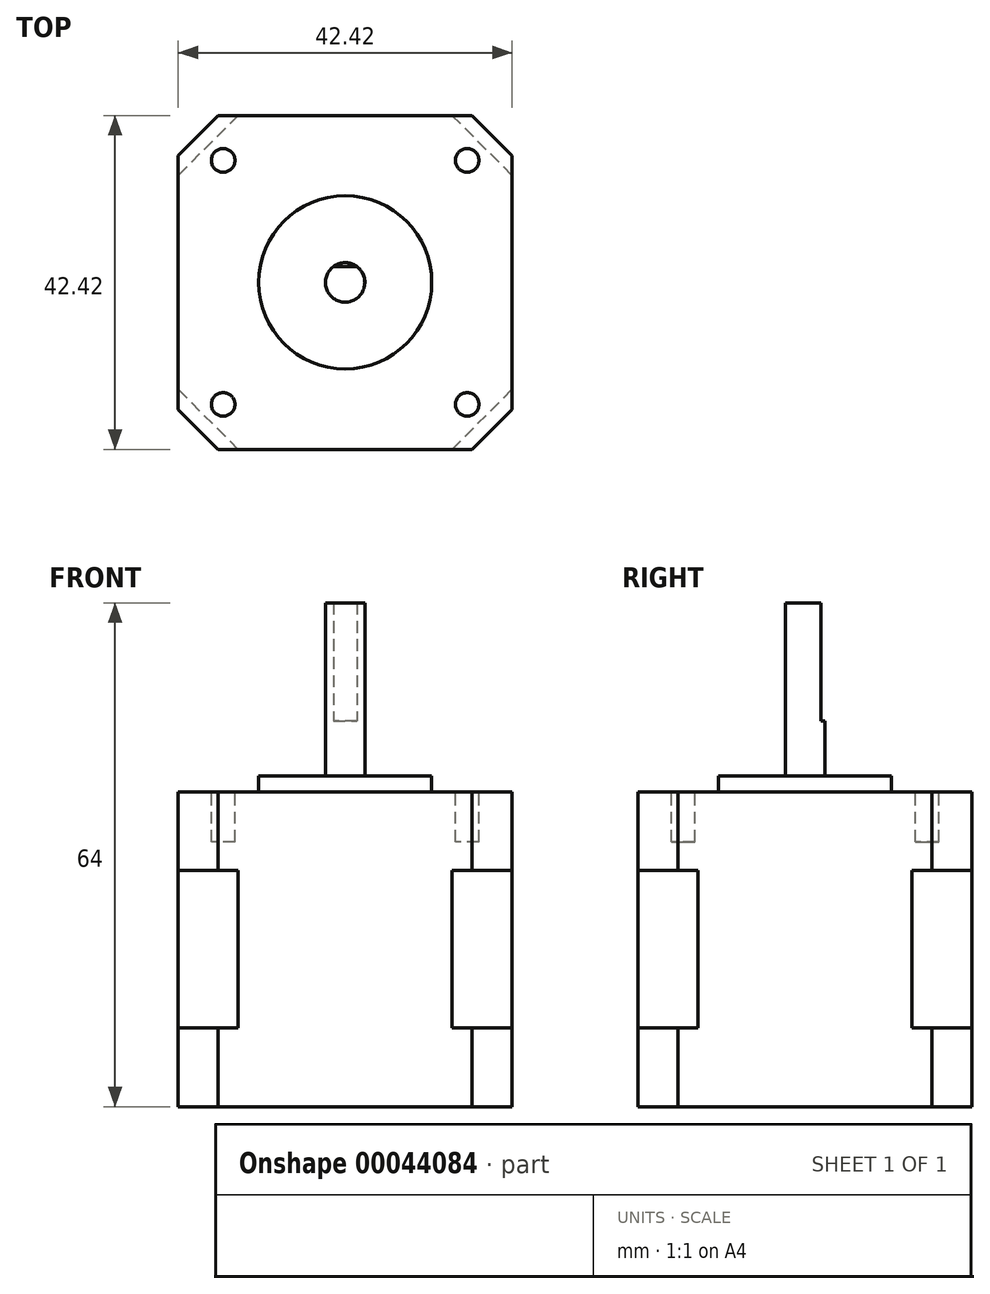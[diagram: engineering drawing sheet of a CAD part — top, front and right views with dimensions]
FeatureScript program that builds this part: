
annotation { "Feature Type Name" : "Feature", "Feature Type Description" : "" }
export const myFeature = defineFeature(function(context is Context, id is Id, definition is map)
    precondition{}
    {
        {
            var Q0;
            Q0=qCreatedBy(makeId("Top.planeOp"),FACE);
            var sketch = newSketch(context, id + "F0", { "sketchPlane" : qUnion([Q0])});
            skLineSegment(sketch, "E0.bottom", {"start": v(-21.2, 21.2) * mm, "end": v(21.2, 21.2) * mm});
            skLineSegment(sketch, "E0.top", {"start": v(-21.2, -21.2) * mm, "end": v(21.2, -21.2) * mm});
            skLineSegment(sketch, "E0.left", {"start": v(-21.2, 21.2) * mm, "end": v(-21.2, -21.2) * mm});
            skLineSegment(sketch, "E0.right", {"start": v(21.2, 21.2) * mm, "end": v(21.2, -21.2) * mm});
            skSolve(sketch);
        }
        {
            var Q0;
            Q0=makeQuery(id+"F0.imprint","IMPRINT",FACE,{"disambiguationData":[TD([[makeQuery(id+"F0.imprint","IMPRINT",EDGE,{"derivedFrom":sQuery(id+"F0.wireOp",EDGE,"E0.bottom")}),-1.0]])]});
            extrude(context, id + "F1", {"entities" : qUnion([Q0]), "depth" : 20 * mm, "symmetric" : true});
        }
        {
            var Q0;
            Q0=makeQuery(id+"F1.opExtrude","SWEPT_EDGE",EDGE,{"disambiguationData":[OSD([sQuery(id+"F0.wireOp",EDGE,"E0.bottom"),sQuery(id+"F0.wireOp",EDGE,"E0.right")])]});
            var Q1;
            Q1=makeQuery(id+"F1.opExtrude","SWEPT_EDGE",EDGE,{"disambiguationData":[OSD([sQuery(id+"F0.wireOp",EDGE,"E0.bottom"),sQuery(id+"F0.wireOp",EDGE,"E0.left")])]});
            var Q2;
            Q2=makeQuery(id+"F1.opExtrude","SWEPT_EDGE",EDGE,{"disambiguationData":[OSD([sQuery(id+"F0.wireOp",EDGE,"E0.top"),sQuery(id+"F0.wireOp",EDGE,"E0.left")])]});
            var Q3;
            Q3=makeQuery(id+"F1.opExtrude","SWEPT_EDGE",EDGE,{"disambiguationData":[OSD([sQuery(id+"F0.wireOp",EDGE,"E0.top"),sQuery(id+"F0.wireOp",EDGE,"E0.right")])]});
            chamfer(context, id + "F2", {"entities" : qUnion([Q0, Q1, Q2, Q3]), "width" : 7.62 * mm, "tangentPropagation" : true});
        }
        {
            var Q0;
            Q0=makeQuery(id+"F1.opExtrude","CAP_FACE",FACE,{"disambiguationData":[OSD([sQuery(id+"F0.wireOp",EDGE,"E0.bottom"),sQuery(id+"F0.wireOp",EDGE,"E0.top"),sQuery(id+"F0.wireOp",EDGE,"E0.left"),sQuery(id+"F0.wireOp",EDGE,"E0.right")])],"isStart":false});
            var sketch = newSketch(context, id + "F3", { "sketchPlane" : qUnion([Q0])});
            skLineSegment(sketch, "E1.bottom", {"start": v(-21.2, 21.2) * mm, "end": v(21.2, 21.2) * mm});
            skLineSegment(sketch, "E1.top", {"start": v(-21.2, -21.2) * mm, "end": v(21.2, -21.2) * mm});
            skLineSegment(sketch, "E1.left", {"start": v(-21.2, 21.2) * mm, "end": v(-21.2, -21.2) * mm});
            skLineSegment(sketch, "E1.right", {"start": v(21.2, 21.2) * mm, "end": v(21.2, -21.2) * mm});
            skSolve(sketch);
        }
        {
            var Q0;
            {var subQ0=sQuery(id+"F0.wireOp",EDGE,"E0.top");var subQ1=sQuery(id+"F0.wireOp",EDGE,"E0.right");var subQ2=sQuery(id+"F0.wireOp",EDGE,"E0.bottom");var subQ3=sQuery(id+"F0.wireOp",EDGE,"E0.left");var subQ4=makeQuery(id+"F1.opExtrude","CAP_FACE",FACE,{"disambiguationData":[OSD([subQ2,subQ0,subQ3,subQ1])],"isStart":false});var subQ8=makeQuery(id+"F2.opChamfer","BLEND_EDGE",EDGE,{"blendedFrom":[makeQuery(id+"F1.opExtrude","SWEPT_EDGE",EDGE,{"disambiguationData":[OSD([subQ2,subQ3])]}),subQ4],"blendedInto":[subQ4]});Q0=makeQuery(id+"F3.imprint","IMPRINT",FACE,{"disambiguationData":[TD([[makeQuery(id+"F3.imprint","IMPRINT",EDGE,{"derivedFrom":subQ8}),1.0]])]});}
            var Q1;
            {var subQ0=sQuery(id+"F0.wireOp",EDGE,"E0.bottom");var subQ1=sQuery(id+"F0.wireOp",EDGE,"E0.right");var subQ2=makeQuery(id+"F2.opChamfer","BLEND_EDGE",EDGE,{"blendedFrom":[makeQuery(id+"F1.opExtrude","SWEPT_EDGE",EDGE,{"disambiguationData":[OSD([subQ0,subQ1])]}),makeQuery(id+"F1.opExtrude","CAP_FACE",FACE,{"disambiguationData":[OSD([subQ0,sQuery(id+"F0.wireOp",EDGE,"E0.top"),sQuery(id+"F0.wireOp",EDGE,"E0.left"),subQ1])],"isStart":false})],"blendedInto":[makeQuery(id+"F1.opExtrude","CAP_FACE",FACE,{"disambiguationData":[OSD([subQ0,sQuery(id+"F0.wireOp",EDGE,"E0.top"),sQuery(id+"F0.wireOp",EDGE,"E0.left"),subQ1])],"isStart":false})]});Q1=makeQuery(id+"F3.imprint","IMPRINT",FACE,{"disambiguationData":[TD([[makeQuery(id+"F3.imprint","IMPRINT",EDGE,{"derivedFrom":subQ2}),-1.0]])]});}
            var Q2;
            {var subQ0=sQuery(id+"F0.wireOp",EDGE,"E0.bottom");var subQ1=sQuery(id+"F0.wireOp",EDGE,"E0.left");var subQ2=makeQuery(id+"F2.opChamfer","BLEND_EDGE",EDGE,{"blendedFrom":[makeQuery(id+"F1.opExtrude","SWEPT_EDGE",EDGE,{"disambiguationData":[OSD([subQ0,subQ1])]}),makeQuery(id+"F1.opExtrude","CAP_FACE",FACE,{"disambiguationData":[OSD([subQ0,sQuery(id+"F0.wireOp",EDGE,"E0.top"),subQ1,sQuery(id+"F0.wireOp",EDGE,"E0.right")])],"isStart":false})],"blendedInto":[makeQuery(id+"F1.opExtrude","CAP_FACE",FACE,{"disambiguationData":[OSD([subQ0,sQuery(id+"F0.wireOp",EDGE,"E0.top"),subQ1,sQuery(id+"F0.wireOp",EDGE,"E0.right")])],"isStart":false})]});Q2=makeQuery(id+"F3.imprint","IMPRINT",FACE,{"disambiguationData":[TD([[makeQuery(id+"F3.imprint","IMPRINT",EDGE,{"derivedFrom":subQ2}),-1.0]])]});}
            var Q3;
            {var subQ0=sQuery(id+"F0.wireOp",EDGE,"E0.top");var subQ1=sQuery(id+"F0.wireOp",EDGE,"E0.left");var subQ2=makeQuery(id+"F2.opChamfer","BLEND_EDGE",EDGE,{"blendedFrom":[makeQuery(id+"F1.opExtrude","SWEPT_EDGE",EDGE,{"disambiguationData":[OSD([subQ0,subQ1])]}),makeQuery(id+"F1.opExtrude","CAP_FACE",FACE,{"disambiguationData":[OSD([sQuery(id+"F0.wireOp",EDGE,"E0.bottom"),subQ0,subQ1,sQuery(id+"F0.wireOp",EDGE,"E0.right")])],"isStart":false})],"blendedInto":[makeQuery(id+"F1.opExtrude","CAP_FACE",FACE,{"disambiguationData":[OSD([sQuery(id+"F0.wireOp",EDGE,"E0.bottom"),subQ0,subQ1,sQuery(id+"F0.wireOp",EDGE,"E0.right")])],"isStart":false})]});Q3=makeQuery(id+"F3.imprint","IMPRINT",FACE,{"disambiguationData":[TD([[makeQuery(id+"F3.imprint","IMPRINT",EDGE,{"derivedFrom":subQ2}),-1.0]])]});}
            var Q4;
            {var subQ0=sQuery(id+"F0.wireOp",EDGE,"E0.top");var subQ1=sQuery(id+"F0.wireOp",EDGE,"E0.right");var subQ2=makeQuery(id+"F2.opChamfer","BLEND_EDGE",EDGE,{"blendedFrom":[makeQuery(id+"F1.opExtrude","SWEPT_EDGE",EDGE,{"disambiguationData":[OSD([subQ0,subQ1])]}),makeQuery(id+"F1.opExtrude","CAP_FACE",FACE,{"disambiguationData":[OSD([sQuery(id+"F0.wireOp",EDGE,"E0.bottom"),subQ0,sQuery(id+"F0.wireOp",EDGE,"E0.left"),subQ1])],"isStart":false})],"blendedInto":[makeQuery(id+"F1.opExtrude","CAP_FACE",FACE,{"disambiguationData":[OSD([sQuery(id+"F0.wireOp",EDGE,"E0.bottom"),subQ0,sQuery(id+"F0.wireOp",EDGE,"E0.left"),subQ1])],"isStart":false})]});Q4=makeQuery(id+"F3.imprint","IMPRINT",FACE,{"disambiguationData":[TD([[makeQuery(id+"F3.imprint","IMPRINT",EDGE,{"derivedFrom":subQ2}),-1.0]])]});}
            extrude(context, id + "F4", {"entities" : qUnion([Q0, Q1, Q2, Q3, Q4]), "operationType" : NewBodyOperationType.ADD, "depth" : 10 * mm});
        }
        {
            var Q0;
            Q0=makeQuery(id+"F4.opExtrude","SWEPT_EDGE",EDGE,{"disambiguationData":[OSD([sQuery(id+"F3.wireOp",EDGE,"E1.bottom"),sQuery(id+"F3.wireOp",EDGE,"E1.right")])]});
            var Q1;
            Q1=makeQuery(id+"F4.opExtrude","SWEPT_EDGE",EDGE,{"disambiguationData":[OSD([sQuery(id+"F3.wireOp",EDGE,"E1.bottom"),sQuery(id+"F3.wireOp",EDGE,"E1.left")])]});
            var Q2;
            Q2=makeQuery(id+"F4.opExtrude","SWEPT_EDGE",EDGE,{"disambiguationData":[OSD([sQuery(id+"F3.wireOp",EDGE,"E1.top"),sQuery(id+"F3.wireOp",EDGE,"E1.left")])]});
            var Q3;
            Q3=makeQuery(id+"F4.opExtrude","SWEPT_EDGE",EDGE,{"disambiguationData":[OSD([sQuery(id+"F3.wireOp",EDGE,"E1.top"),sQuery(id+"F3.wireOp",EDGE,"E1.right")])]});
            chamfer(context, id + "F5", {"entities" : qUnion([Q0, Q1, Q2, Q3]), "width" : 5.08 * mm, "tangentPropagation" : true});
        }
        {
            var Q0;
            Q0=makeQuery(id+"F1.opExtrude","CAP_FACE",FACE,{"disambiguationData":[OSD([sQuery(id+"F0.wireOp",EDGE,"E0.bottom"),sQuery(id+"F0.wireOp",EDGE,"E0.top"),sQuery(id+"F0.wireOp",EDGE,"E0.left"),sQuery(id+"F0.wireOp",EDGE,"E0.right")])],"isStart":true});
            var sketch = newSketch(context, id + "F6", { "sketchPlane" : qUnion([Q0])});
            skLineSegment(sketch, "E2.0.0", {"start": v(-16.13, 21.2) * mm, "end": v(16.13, 21.2) * mm});
            skLineSegment(sketch, "E2.0.1", {"start": v(16.13, 21.2) * mm, "end": v(21.2, 16.13) * mm});
            skLineSegment(sketch, "E2.0.2", {"start": v(21.2, -16.13) * mm, "end": v(21.2, 16.13) * mm});
            skLineSegment(sketch, "E2.0.3", {"start": v(21.2, -16.13) * mm, "end": v(16.13, -21.2) * mm});
            skLineSegment(sketch, "E2.0.4", {"start": v(-16.13, -21.2) * mm, "end": v(16.13, -21.2) * mm});
            skLineSegment(sketch, "E2.0.5", {"start": v(-16.13, -21.2) * mm, "end": v(-21.2, -16.13) * mm});
            skLineSegment(sketch, "E2.0.6", {"start": v(-21.2, -16.13) * mm, "end": v(-21.2, 16.13) * mm});
            skLineSegment(sketch, "E2.0.7", {"start": v(-21.2, 16.13) * mm, "end": v(-16.13, 21.2) * mm});
            skSolve(sketch);
        }
        {
            var Q0;
            {var subQ3=sQuery(id+"F6.wireOp",EDGE,"E2.0.7");Q0=makeQuery(id+"F6.imprint","IMPRINT",FACE,{"disambiguationData":[TD([[makeQuery(id+"F6.imprint","IMPRINT",EDGE,{"derivedFrom":subQ3}),-1.0]])]});}
            var Q1;
            {var subQ4=sQuery(id+"F6.wireOp",EDGE,"E2.0.1");Q1=makeQuery(id+"F6.imprint","IMPRINT",FACE,{"disambiguationData":[TD([[makeQuery(id+"F6.imprint","IMPRINT",EDGE,{"derivedFrom":subQ4}),-1.0]])]});}
            var Q2;
            {var subQ4=sQuery(id+"F6.wireOp",EDGE,"E2.0.3");Q2=makeQuery(id+"F6.imprint","IMPRINT",FACE,{"disambiguationData":[TD([[makeQuery(id+"F6.imprint","IMPRINT",EDGE,{"derivedFrom":subQ4}),-1.0]])]});}
            var Q3;
            {var subQ4=sQuery(id+"F6.wireOp",EDGE,"E2.0.5");Q3=makeQuery(id+"F6.imprint","IMPRINT",FACE,{"disambiguationData":[TD([[makeQuery(id+"F6.imprint","IMPRINT",EDGE,{"derivedFrom":subQ4}),-1.0]])]});}
            var Q4;
            {var subQ0=sQuery(id+"F0.wireOp",EDGE,"E0.top");var subQ1=sQuery(id+"F0.wireOp",EDGE,"E0.right");var subQ2=sQuery(id+"F0.wireOp",EDGE,"E0.bottom");var subQ3=sQuery(id+"F0.wireOp",EDGE,"E0.left");var subQ4=makeQuery(id+"F1.opExtrude","CAP_FACE",FACE,{"disambiguationData":[OSD([subQ2,subQ0,subQ3,subQ1])],"isStart":true});var subQ8=makeQuery(id+"F2.opChamfer","BLEND_EDGE",EDGE,{"blendedFrom":[makeQuery(id+"F1.opExtrude","SWEPT_EDGE",EDGE,{"disambiguationData":[OSD([subQ2,subQ3])]}),subQ4],"blendedInto":[subQ4]});Q4=makeQuery(id+"F6.imprint","IMPRINT",FACE,{"disambiguationData":[TD([[makeQuery(id+"F6.imprint","IMPRINT",EDGE,{"derivedFrom":subQ8}),1.0]])]});}
            extrude(context, id + "F7", {"entities" : qUnion([Q0, Q1, Q2, Q3, Q4]), "operationType" : NewBodyOperationType.ADD, "depth" : 10 * mm});
        }
        {
            var Q0;
            Q0=makeQuery(id+"F4.opExtrude","CAP_FACE",FACE,{"disambiguationData":[OSD([sQuery(id+"F3.wireOp",EDGE,"E1.bottom"),sQuery(id+"F3.wireOp",EDGE,"E1.top"),sQuery(id+"F3.wireOp",EDGE,"E1.left"),sQuery(id+"F3.wireOp",EDGE,"E1.right")])],"isStart":false});
            var sketch = newSketch(context, id + "F8", { "sketchPlane" : qUnion([Q0])});
            skCircle(sketch, "E3", {"center": v(0, 0) * mm, "radius": 11 * mm});
            skSolve(sketch);
        }
        {
            var Q0;
            Q0=makeQuery(id+"F8.imprint","IMPRINT",FACE,{"disambiguationData":[TD([[makeQuery(id+"F8.imprint","IMPRINT",EDGE,{"derivedFrom":sQuery(id+"F8.wireOp",EDGE,"E3")}),1.0]])]});
            extrude(context, id + "F9", {"entities" : qUnion([Q0]), "operationType" : NewBodyOperationType.ADD, "depth" : 2 * mm});
        }
        {
            var Q0;
            Q0=makeQuery(id+"F9.opExtrude","CAP_FACE",FACE,{"disambiguationData":[OSD([sQuery(id+"F8.wireOp",EDGE,"E3")])],"isStart":false});
            var sketch = newSketch(context, id + "F10", { "sketchPlane" : qUnion([Q0])});
            skCircle(sketch, "E4", {"center": v(0, 0) * mm, "radius": 2.5 * mm});
            skSolve(sketch);
        }
        {
            var Q0;
            Q0=makeQuery(id+"F10.imprint","IMPRINT",FACE,{"disambiguationData":[TD([[makeQuery(id+"F10.imprint","IMPRINT",EDGE,{"derivedFrom":sQuery(id+"F10.wireOp",EDGE,"E4")}),1.0]])]});
            extrude(context, id + "F11", {"entities" : qUnion([Q0]), "operationType" : NewBodyOperationType.ADD, "depth" : 22 * mm});
        }
        {
            var Q0;
            Q0=makeQuery(id+"F11.opExtrude","CAP_FACE",FACE,{"disambiguationData":[OSD([sQuery(id+"F10.wireOp",EDGE,"E4")])],"isStart":false});
            var sketch = newSketch(context, id + "F12", { "sketchPlane" : qUnion([Q0])});
            skLineSegment(sketch, "E5.bottom", {"start": v(-2.63, 2.93) * mm, "end": v(2.62, 2.93) * mm});
            skLineSegment(sketch, "E5.top", {"start": v(-2.63, 2) * mm, "end": v(2.62, 2) * mm});
            skLineSegment(sketch, "E5.left", {"start": v(-2.63, 2.93) * mm, "end": v(-2.63, 2) * mm});
            skLineSegment(sketch, "E5.right", {"start": v(2.62, 2.93) * mm, "end": v(2.62, 2) * mm});
            skSolve(sketch);
        }
        {
            var Q0;
            {var subQ0=makeQuery(id+"F11.opExtrude","CAP_EDGE",EDGE,{"disambiguationData":[OSD([sQuery(id+"F10.wireOp",EDGE,"E4")])],"isStart":false});var subQ1=sQuery(id+"F12.wireOp",EDGE,"E5.top");var subQ3=makeQuery(id+"F12.imprint","INTERSECT",VERTEX,{"disambiguationData":[OD(0.0)],"derivedFrom":[subQ0,subQ1]});Q0=qUnion([makeQuery(id+"F12.imprint","IMPRINT",FACE,{"disambiguationData":[TD([[makeQuery(id+"F12.imprint","IMPRINT",EDGE,{"derivedFrom":sQuery(id+"F12.wireOp",EDGE,"E5.bottom")}),-1.0]])]}),makeQuery(id+"F12.imprint","IMPRINT",FACE,{"disambiguationData":[TD([[makeQuery(id+"F12.imprint","IMPRINT",EDGE,{"disambiguationData":[TD([[subQ3,-1.0]])],"derivedFrom":subQ1}),1.0]])]})]);}
            extrude(context, id + "F13", {"entities" : qUnion([Q0]), "operationType" : NewBodyOperationType.REMOVE, "oppositeDirection" : true, "depth" : 15 * mm});
        }
        {
            var Q0;
            Q0=makeQuery(id+"F4.opExtrude","CAP_FACE",FACE,{"disambiguationData":[OSD([sQuery(id+"F3.wireOp",EDGE,"E1.bottom"),sQuery(id+"F3.wireOp",EDGE,"E1.top"),sQuery(id+"F3.wireOp",EDGE,"E1.left"),sQuery(id+"F3.wireOp",EDGE,"E1.right")])],"isStart":false});
            var sketch = newSketch(context, id + "F14", { "sketchPlane" : qUnion([Q0])});
            skCircle(sketch, "E6", {"center": v(-15.5, 15.5) * mm, "radius": 1.5 * mm});
            skCircle(sketch, "E7", {"center": v(15.5, 15.5) * mm, "radius": 1.5 * mm});
            skCircle(sketch, "E8", {"center": v(15.5, -15.5) * mm, "radius": 1.5 * mm});
            skCircle(sketch, "E9", {"center": v(-15.5, -15.5) * mm, "radius": 1.5 * mm});
            skLineSegment(sketch, "E10", {"start": v(-45.53, 0) * mm, "end": v(50.04, 0) * mm, "construction": true});
            skLineSegment(sketch, "E11", {"start": v(0, -35.63) * mm, "end": v(0, 35.98) * mm, "construction": true});
            skLineSegment(sketch, "E12.rect.bottom", {"start": v(-15.5, 15.5) * mm, "end": v(15.5, 15.5) * mm, "construction": true});
            skLineSegment(sketch, "E12.rect.top", {"start": v(-15.5, -15.5) * mm, "end": v(15.5, -15.5) * mm, "construction": true});
            skLineSegment(sketch, "E12.rect.left", {"start": v(-15.5, 15.5) * mm, "end": v(-15.5, -15.5) * mm, "construction": true});
            skLineSegment(sketch, "E12.rect.right", {"start": v(15.5, 15.5) * mm, "end": v(15.5, -15.5) * mm, "construction": true});
            skPoint(sketch, "E12.rect.middle", {"position": v(0, 0) * mm});
            skPoint(sketch, "E13", {"position": v(0, 15.5) * mm});
            skSolve(sketch);
        }
        {
            var Q0;
            {Q0=qUnion([makeQuery(id+"F14.imprint","IMPRINT",FACE,{"disambiguationData":[TD([[makeQuery(id+"F14.imprint","IMPRINT",EDGE,{"derivedFrom":sQuery(id+"F14.wireOp",EDGE,"E6")}),1.0]])]}),makeQuery(id+"F14.imprint","IMPRINT",FACE,{"disambiguationData":[TD([[makeQuery(id+"F14.imprint","IMPRINT",EDGE,{"derivedFrom":sQuery(id+"F14.wireOp",EDGE,"E7")}),1.0]])]}),makeQuery(id+"F14.imprint","IMPRINT",FACE,{"disambiguationData":[TD([[makeQuery(id+"F14.imprint","IMPRINT",EDGE,{"derivedFrom":sQuery(id+"F14.wireOp",EDGE,"E8")}),1.0]])]}),makeQuery(id+"F14.imprint","IMPRINT",FACE,{"disambiguationData":[TD([[makeQuery(id+"F14.imprint","IMPRINT",EDGE,{"derivedFrom":sQuery(id+"F14.wireOp",EDGE,"E9")}),1.0]])]})]);}
            extrude(context, id + "F15", {"entities" : qUnion([Q0]), "operationType" : NewBodyOperationType.REMOVE, "oppositeDirection" : true, "depth" : 6.35 * mm});
        }
    });
